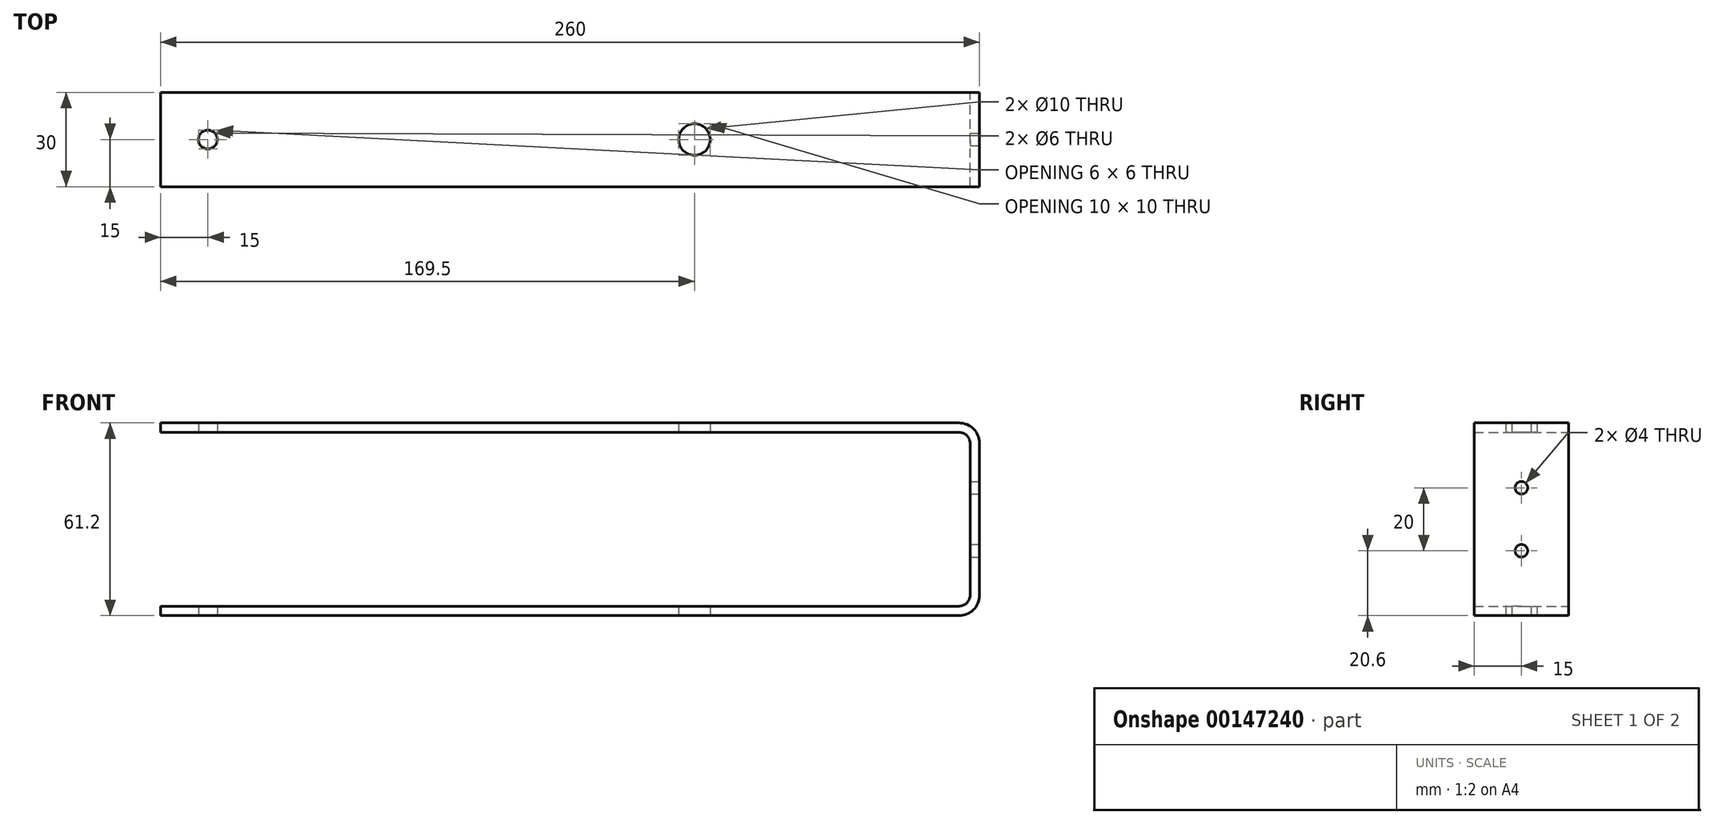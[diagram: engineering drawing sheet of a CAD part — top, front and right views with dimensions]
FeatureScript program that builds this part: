
annotation { "Feature Type Name" : "Feature", "Feature Type Description" : "" }
export const myFeature = defineFeature(function(context is Context, id is Id, definition is map)
    precondition{}
    {
        {
            var Q0;
            Q0=qCreatedBy(makeId("Front.planeOp"),FACE);
            var sketch = newSketch(context, id + "F0", { "sketchPlane" : qUnion([Q0])});
            skLineSegment(sketch, "E0", {"start": v(-258.5, 29.1) * mm, "end": v(-5, 29.1) * mm});
            skLineSegment(sketch, "E1", {"start": v(0, 24.1) * mm, "end": v(0, -24.1) * mm});
            skLineSegment(sketch, "E2", {"start": v(-5, -29.1) * mm, "end": v(-258.5, -29.1) * mm});
            skPoint(sketch, "E3.visualSharp", {"position": v(0, 29.1) * mm});
            skArc(sketch, "E3.filletArc", {"start": v(0, 24.1) * mm, "mid": v(-1.46, 27.64) * mm, "end": v(-5, 29.1) * mm});
            skPoint(sketch, "E4.visualSharp", {"position": v(0, -29.1) * mm});
            skArc(sketch, "E4.filletArc", {"start": v(-5, -29.1) * mm, "mid": v(-1.46, -27.64) * mm, "end": v(0, -24.1) * mm});
            skSolve(sketch);
        }
        {
            var Q0;
            Q0=qCreatedBy(makeId("Right.planeOp"),FACE);
            var Q1;
            Q1=sQuery(id+"F0.wireOp",VERTEX,"E0.start");
            cPlane(context, id + "F1", {"entities" : qUnion([Q0, Q1]), "cplaneType" : CPlaneType.PLANE_POINT, "offset" : 25 * mm, "width" : 150 * mm, "height" : 150 * mm});
        }
        {
            var Q0;
            Q0=qCreatedBy(id+"F1.planeOp",FACE);
            var sketch = newSketch(context, id + "F2", { "sketchPlane" : qUnion([Q0])});
            skLineSegment(sketch, "E5.bottom", {"start": v(-15, 27.6) * mm, "end": v(15, 27.6) * mm});
            skLineSegment(sketch, "E5.top", {"start": v(-15, 30.6) * mm, "end": v(15, 30.6) * mm});
            skLineSegment(sketch, "E5.left", {"start": v(-15, 27.6) * mm, "end": v(-15, 30.6) * mm});
            skLineSegment(sketch, "E5.right", {"start": v(15, 27.6) * mm, "end": v(15, 30.6) * mm});
            skPoint(sketch, "E5.middle", {"position": v(0, 29.1) * mm});
            skSolve(sketch);
        }
        {
            var Q0;
            Q0 = qSketchRegion(id + "F2", true);
            var Q1;
            Q1 = qConstructionFilter(qBodyType(qCreatedBy(id + "F0" ,EDGE), BodyType.WIRE), ConstructionObject.NO);
            sweep(context, id + "F3", {"profiles" : qUnion([Q0]), "path" : qUnion([Q1])});
        }
        {
            var Q0;
            Q0=makeQuery(id+"F3.opSweep","SWEPT_FACE",FACE,{"disambiguationData":[OSD([sQuery(id+"F0.wireOp",EDGE,"E2"),sQuery(id+"F2.wireOp",EDGE,"E5.top")])]});
            var sketch = newSketch(context, id + "F4", { "sketchPlane" : qUnion([Q0])});
            skCircle(sketch, "E6", {"center": v(-89, 0) * mm, "radius": 5 * mm});
            skLineSegment(sketch, "E7", {"start": v(-89, 0) * mm, "end": v(0, 0) * mm});
            skSolve(sketch);
        }
        {
            var Q0;
            Q0 = qSketchRegion(id + "F4", true);
            extrude(context, id + "F5", {"entities" : qUnion([Q0]), "operationType" : NewBodyOperationType.REMOVE, "endBound" : BoundingType.THROUGH_ALL, "oppositeDirection" : true, "depth" : 25 * mm});
        }
        {
            var Q0;
            Q0=makeQuery(id+"F3.opSweep","SWEPT_FACE",FACE,{"disambiguationData":[OSD([sQuery(id+"F0.wireOp",EDGE,"E1"),sQuery(id+"F2.wireOp",EDGE,"E5.top")])]});
            var sketch = newSketch(context, id + "F6", { "sketchPlane" : qUnion([Q0])});
            skCircle(sketch, "E8", {"center": v(0, 10) * mm, "radius": 2 * mm});
            skCircle(sketch, "E9", {"center": v(0, -10) * mm, "radius": 2 * mm});
            skLineSegment(sketch, "E10", {"start": v(0, 10) * mm, "end": v(0, -10) * mm, "construction": true});
            skSolve(sketch);
        }
        {
            var Q0;
            Q0 = qSketchRegion(id + "F6", true);
            extrude(context, id + "F7", {"entities" : qUnion([Q0]), "operationType" : NewBodyOperationType.REMOVE, "endBound" : BoundingType.THROUGH_ALL, "oppositeDirection" : true, "depth" : 25 * mm});
        }
        {
            var Q0;
            Q0=makeQuery(id+"F3.opSweep","SWEPT_FACE",FACE,{"disambiguationData":[OSD([sQuery(id+"F0.wireOp",EDGE,"E2"),sQuery(id+"F2.wireOp",EDGE,"E5.top")])]});
            var sketch = newSketch(context, id + "F8", { "sketchPlane" : qUnion([Q0])});
            skCircle(sketch, "E11", {"center": v(-243.5, 0) * mm, "radius": 3 * mm});
            skLineSegment(sketch, "E12", {"start": v(0, 0) * mm, "end": v(-243.5, 0) * mm, "construction": true});
            skSolve(sketch);
        }
        {
            var Q0;
            Q0 = qSketchRegion(id + "F8", true);
            extrude(context, id + "F9", {"entities" : qUnion([Q0]), "operationType" : NewBodyOperationType.REMOVE, "endBound" : BoundingType.THROUGH_ALL, "oppositeDirection" : true, "depth" : 25 * mm});
        }
    });
